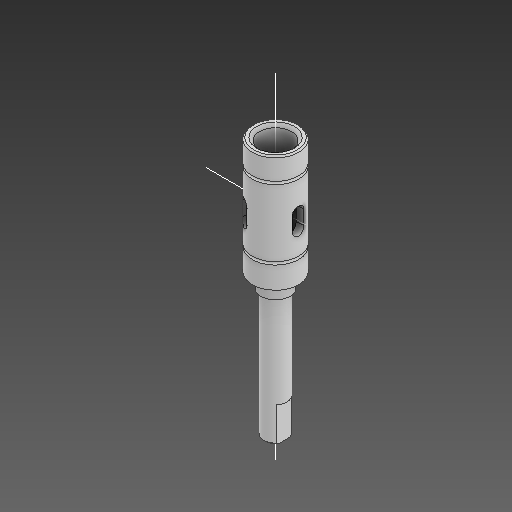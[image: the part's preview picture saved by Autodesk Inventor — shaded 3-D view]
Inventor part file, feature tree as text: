
AUTODESK INVENTOR PART (.ipt)
format: ipt  version: 2021 (Build 250183000, 183)  size: 227,328 bytes
history: native  units: in
note: dims shown in document units (in); Inventor stores cm internally (conversion verified against a paired STEP export)
features: sketch x10, other x8, plane x3
ambient origin geometry x8: Origin, YZ Plane, XZ Plane, XY Plane, X Axis, Y Axis, Z Axis, Center Point
bodies: Solid1 (feature_tree)
feature tree (21):
  other  "iner_sleeve.ipt"
  other  "Solid1::iner_sleeve.ipt"
  other  "TaggingFeature1"
  sketch  "Sketch1"  dims[d0=0.3937in]
  sketch  "Sketch2"
  sketch  "Sketch3"
  sketch  "Sketch5"
  sketch  "Sketch6"
  sketch  "Sketch7"
  sketch  "Sketch8"
  sketch  "Sketch10"
  sketch  "Sketch11"
  sketch  "Sketch12"
  plane  "Work Plane1"
  plane  "Work Plane2"
  plane  "Work Plane3"
  other  "Work Axis1"
  other  "Work Axis2"
  other  "Work Axis3"
  other  "Srf1"
  other  "Srf1::Derived"
